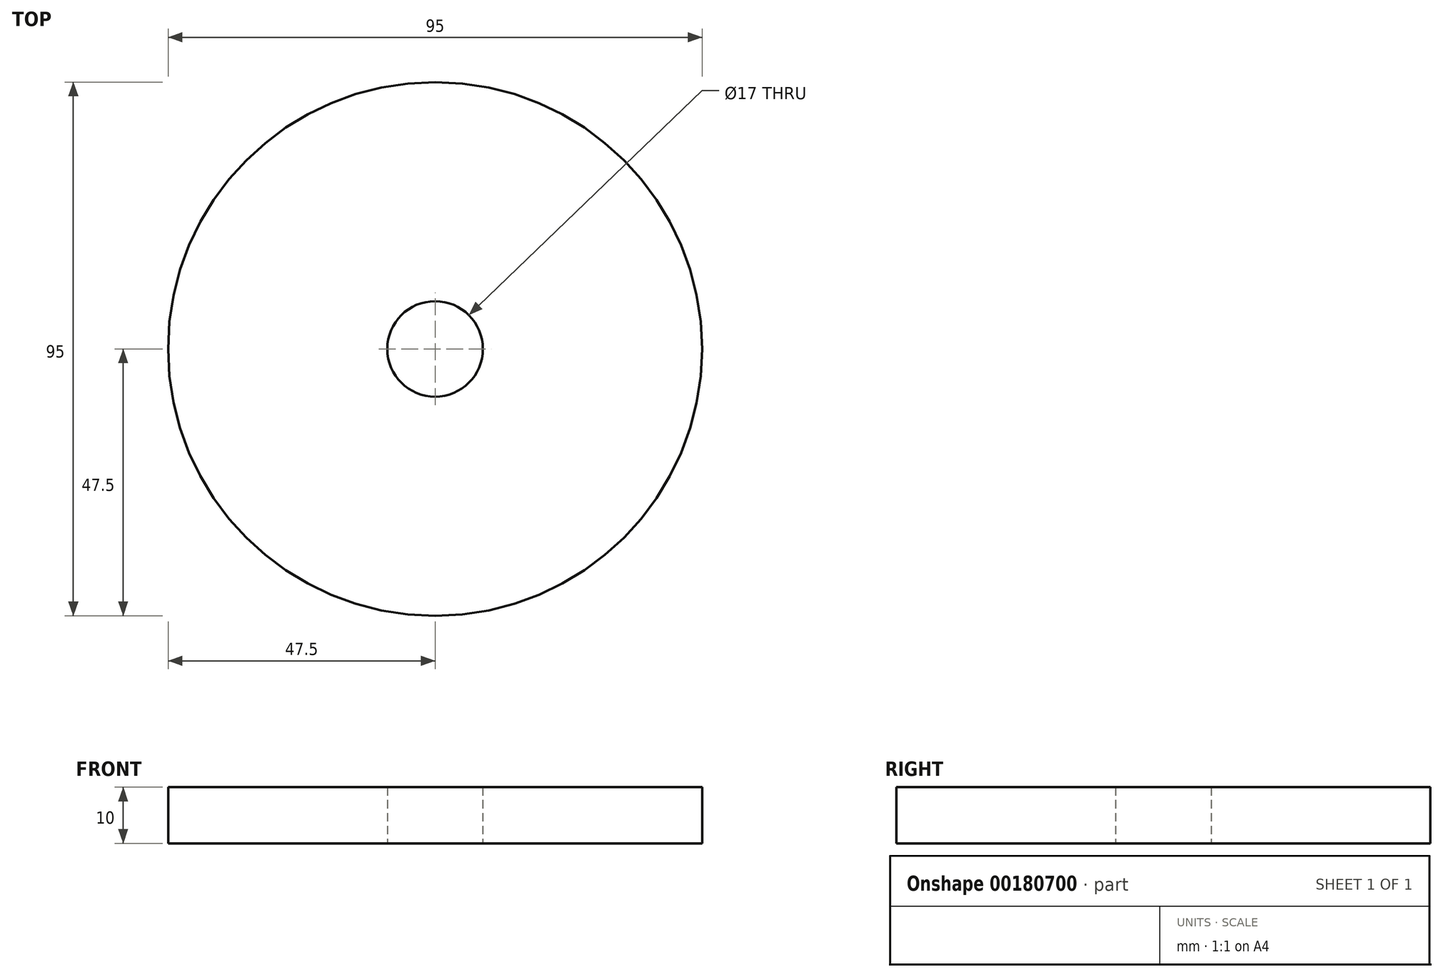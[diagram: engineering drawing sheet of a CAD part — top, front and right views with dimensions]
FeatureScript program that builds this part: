
annotation { "Feature Type Name" : "Feature", "Feature Type Description" : "" }
export const myFeature = defineFeature(function(context is Context, id is Id, definition is map)
    precondition{}
    {
        {
            var Q0;
            Q0=qCreatedBy(makeId("Top.planeOp"),FACE);
            var sketch = newSketch(context, id + "F0", { "sketchPlane" : qUnion([Q0])});
            skCircle(sketch, "E0", {"center": v(0, 0) * mm, "radius": 47.5 * mm});
            skCircle(sketch, "E1", {"center": v(0, 0) * mm, "radius": 8.5 * mm});
            skSolve(sketch);
        }
        {
            var Q0;
            Q0=makeQuery(id+"F0.imprint","IMPRINT",FACE,{"disambiguationData":[TD([[makeQuery(id+"F0.imprint","IMPRINT",EDGE,{"derivedFrom":sQuery(id+"F0.wireOp",EDGE,"E0")}),1.0]])]});
            extrude(context, id + "F1", {"entities" : qUnion([Q0]), "depth" : 10 * mm});
        }
    });
